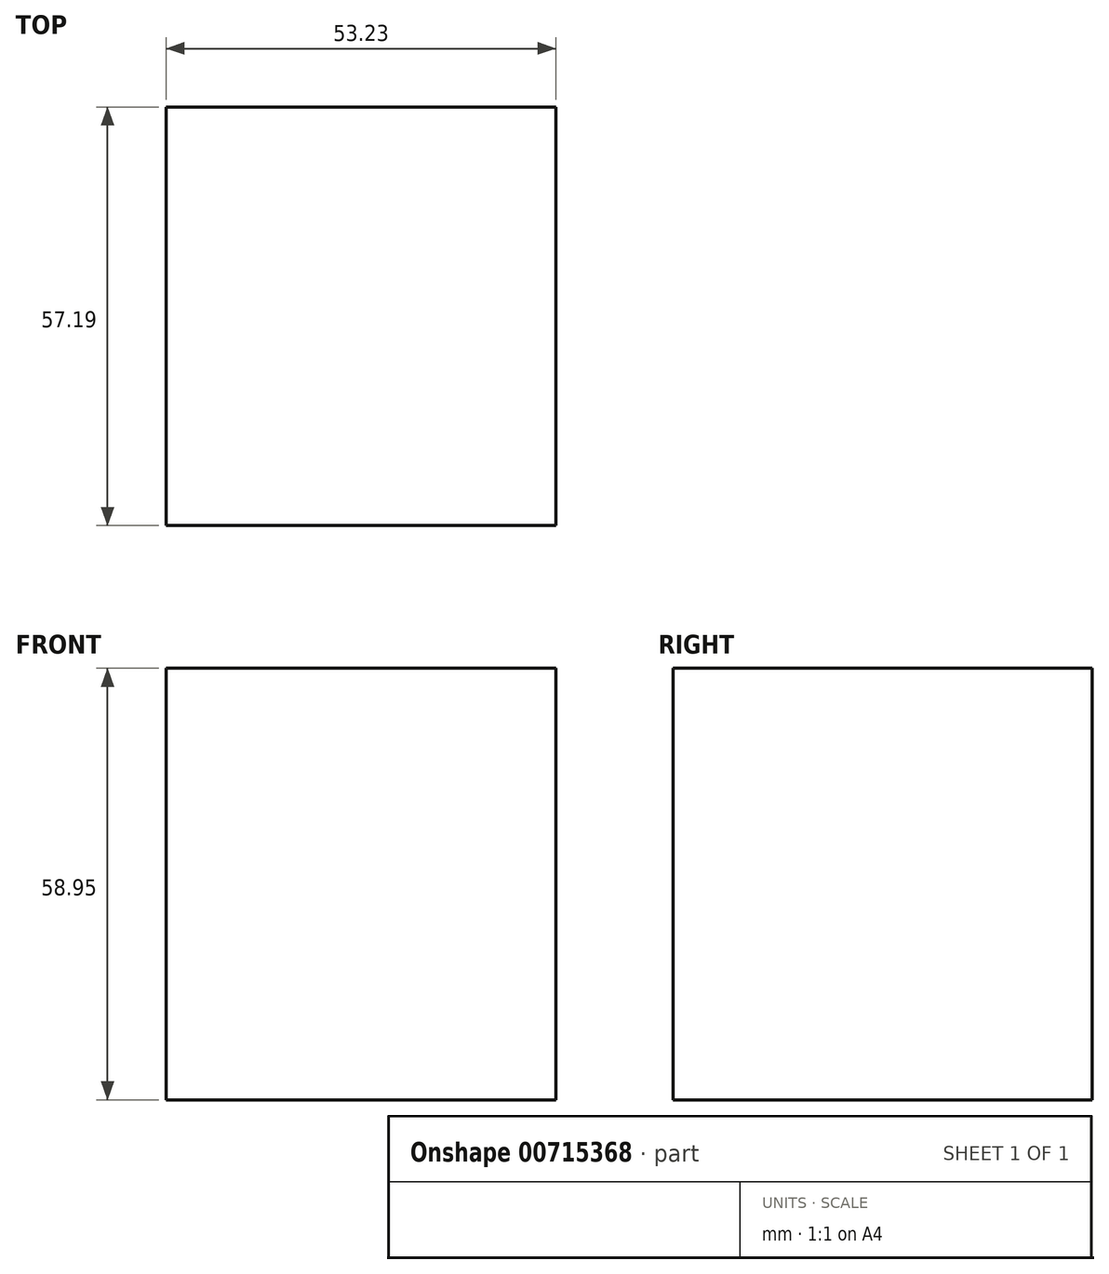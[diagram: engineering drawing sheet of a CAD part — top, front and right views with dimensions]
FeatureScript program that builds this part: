
annotation { "Feature Type Name" : "Feature", "Feature Type Description" : "" }
export const myFeature = defineFeature(function(context is Context, id is Id, definition is map)
    precondition{}
    {
        {
            var Q0;
            Q0=qCreatedBy(makeId("Top.planeOp"),FACE);
            var sketch = newSketch(context, id + "F0", { "sketchPlane" : qUnion([Q0])});
            skLineSegment(sketch, "E0.bottom", {"start": v(-27.91, 15.14) * mm, "end": v(25.32, 15.14) * mm});
            skLineSegment(sketch, "E0.top", {"start": v(-27.91, -42.05) * mm, "end": v(25.32, -42.05) * mm});
            skLineSegment(sketch, "E0.left", {"start": v(-27.91, 15.14) * mm, "end": v(-27.91, -42.05) * mm});
            skLineSegment(sketch, "E0.right", {"start": v(25.32, 15.14) * mm, "end": v(25.32, -42.05) * mm});
            skSolve(sketch);
        }
        {
            var Q0;
            Q0 = qSketchRegion(id + "F0", true);
            extrude(context, id + "F1", {"entities" : qUnion([Q0]), "depth" : 58.95 * mm, "offsetDistance" : 25.4 * mm});
        }
    });
